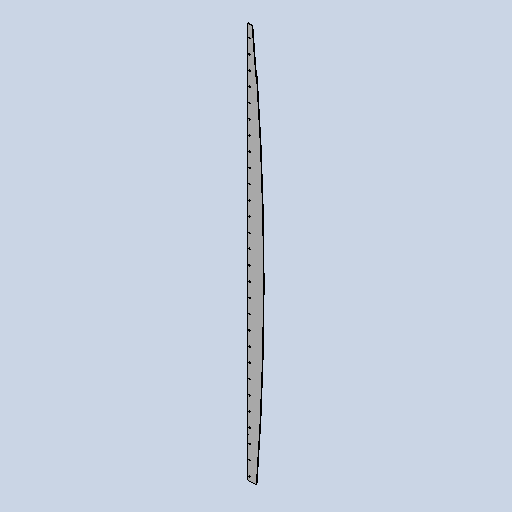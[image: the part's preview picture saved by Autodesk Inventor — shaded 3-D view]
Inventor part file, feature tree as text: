
AUTODESK INVENTOR PART (.ipt)
format: ipt  version: 2025 (Build 290162010, 162A)  size: 236,032 bytes
history: native  units: mm
features: sketch x2, other x2, sheet_metal_op x1, extrude x1, pattern_linear x1, projected_geometry x1
ambient origin geometry x8: Origin, YZ Plane, XZ Plane, XY Plane, X Axis, Y Axis, Z Axis, Center Point
bodies: Body1 (feature_tree)
feature tree (8):
  sheet_metal_op  "Face1"
  extrude  "Extrusion2"  Depth=3.0mm
  pattern_linear  "Rectangular Pattern1"  Spacing1=3.0mm  [1 undecoded]
  sketch  "Sketch1"  dims[d65=8.0mm d78=3.0mm]
  other  "Plate3"
  sketch  "Sketch3"  dims[d80=3.0mm d115=3.0mm d120=3.0mm d131=11050.0mm d132=25.0mm d133=42.0mm d134=1970.0mm d135=7.0mm d136=8.0mm d137=20.0mm d138=10.0mm d139=0.0mm d140=310.0mm d142=70.0mm d143=10.0mm d145=4.0mm d146=210.0mm d147=4.0mm]
  projected_geometry  "Projected Loop1"
  other  "Definition1"
note: 1 required parameter value undecoded (feature->parameter linkage not recoverable at this tier; creation-order binding heuristic only, values carry confidence <= 0.55)
